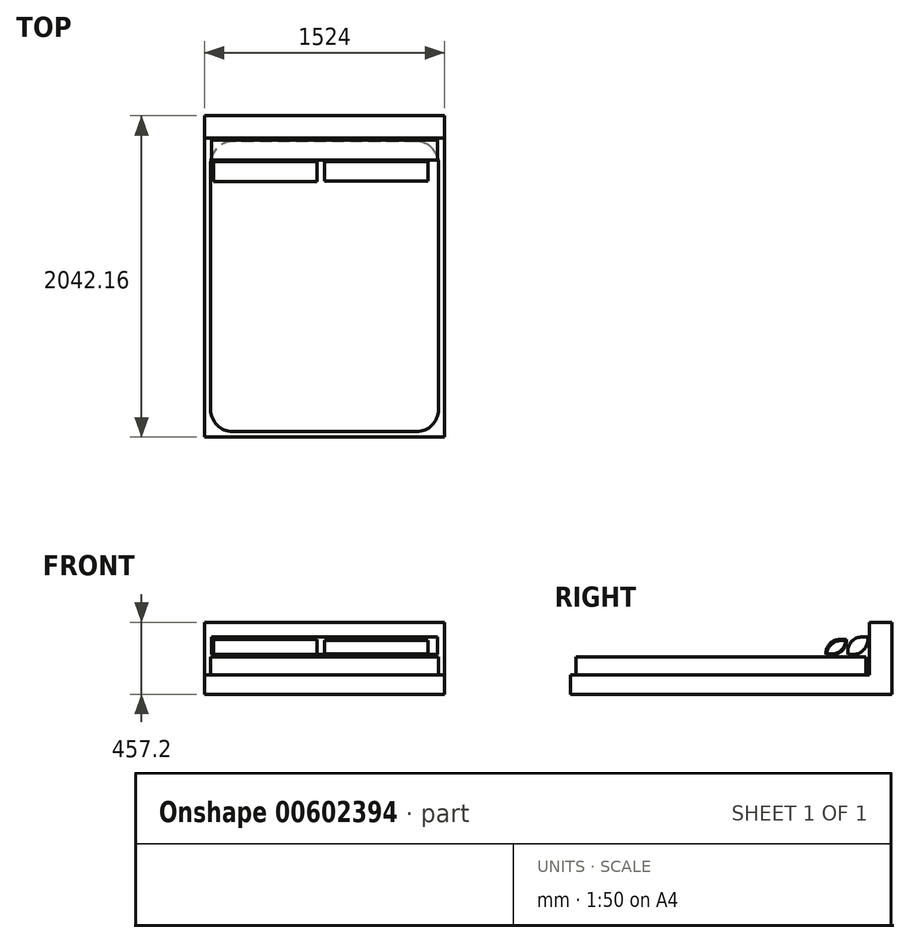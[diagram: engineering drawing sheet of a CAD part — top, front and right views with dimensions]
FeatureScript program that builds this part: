
annotation { "Feature Type Name" : "Feature", "Feature Type Description" : "" }
export const myFeature = defineFeature(function(context is Context, id is Id, definition is map)
    precondition{}
    {
        {
            var Q0;
            Q0=qCreatedBy(makeId("Top.planeOp"),FACE);
            var sketch = newSketch(context, id + "F0", { "sketchPlane" : qUnion([Q0])});
            skLineSegment(sketch, "E0.bottom", {"start": v(-762, 1021.08) * mm, "end": v(762, 1021.08) * mm});
            skLineSegment(sketch, "E0.top", {"start": v(-762, -1021.08) * mm, "end": v(762, -1021.08) * mm});
            skLineSegment(sketch, "E0.left", {"start": v(-762, 1021.08) * mm, "end": v(-762, -1021.08) * mm});
            skLineSegment(sketch, "E0.right", {"start": v(762, 1021.08) * mm, "end": v(762, -1021.08) * mm});
            skPoint(sketch, "E0.middle", {"position": v(0, 0) * mm});
            skSolve(sketch);
        }
        {
            var Q0;
            Q0=makeQuery(id+"F0.imprint","IMPRINT",FACE,{"disambiguationData":[TD([[makeQuery(id+"F0.imprint","IMPRINT",EDGE,{"derivedFrom":sQuery(id+"F0.wireOp",EDGE,"E0.bottom")}),-1.0]])]});
            extrude(context, id + "F1", {"entities" : qUnion([Q0]), "depth" : 121.92 * mm, "offsetDistance" : 30.48 * mm});
        }
        {
            var Q0;
            Q0=makeQuery(id+"F1.opExtrude","CAP_FACE",FACE,{"disambiguationData":[OSD([sQuery(id+"F0.wireOp",EDGE,"E0.bottom"),sQuery(id+"F0.wireOp",EDGE,"E0.top"),sQuery(id+"F0.wireOp",EDGE,"E0.left"),sQuery(id+"F0.wireOp",EDGE,"E0.right")])],"isStart":false});
            var sketch = newSketch(context, id + "F2", { "sketchPlane" : qUnion([Q0])});
            skPoint(sketch, "E1.middle", {"position": v(0, 0) * mm});
            skLineSegment(sketch, "E2.bottom", {"start": v(723.49, -985.48) * mm, "end": v(-723.49, -985.48) * mm});
            skLineSegment(sketch, "E2.top", {"start": v(723.49, 856.5) * mm, "end": v(-723.49, 856.5) * mm});
            skLineSegment(sketch, "E2.left", {"start": v(723.49, -985.48) * mm, "end": v(723.49, 856.5) * mm});
            skLineSegment(sketch, "E2.right", {"start": v(-723.49, -985.48) * mm, "end": v(-723.49, 856.5) * mm});
            skSolve(sketch);
        }
        {
            var Q0;
            Q0=makeQuery(id+"F2.imprint","IMPRINT",FACE,{"disambiguationData":[TD([[makeQuery(id+"F2.imprint","IMPRINT",EDGE,{"derivedFrom":sQuery(id+"F2.wireOp",EDGE,"E2.bottom")}),-1.0]])]});
            extrude(context, id + "F3", {"entities" : qUnion([Q0]), "operationType" : NewBodyOperationType.ADD, "depth" : 114.3 * mm, "offsetDistance" : 30.48 * mm});
        }
        {
            var Q0;
            Q0=makeQuery(id+"F3.opExtrude","SWEPT_EDGE",EDGE,{"disambiguationData":[OSD([sQuery(id+"F2.wireOp",EDGE,"E2.top"),sQuery(id+"F2.wireOp",EDGE,"E2.right")])]});
            var Q1;
            Q1=makeQuery(id+"F3.opExtrude","SWEPT_EDGE",EDGE,{"disambiguationData":[OSD([sQuery(id+"F2.wireOp",EDGE,"E2.top"),sQuery(id+"F2.wireOp",EDGE,"E2.left")])]});
            var Q2;
            Q2=makeQuery(id+"F3.opExtrude","SWEPT_EDGE",EDGE,{"disambiguationData":[OSD([sQuery(id+"F2.wireOp",EDGE,"E2.bottom"),sQuery(id+"F2.wireOp",EDGE,"E2.left")])]});
            var Q3;
            Q3=makeQuery(id+"F3.opExtrude","SWEPT_EDGE",EDGE,{"disambiguationData":[OSD([sQuery(id+"F2.wireOp",EDGE,"E2.bottom"),sQuery(id+"F2.wireOp",EDGE,"E2.right")])]});
            fillet(context, id + "F4", {"entities" : qUnion([Q0, Q1, Q2, Q3]), "radius" : 139.8 * mm, "tangentPropagation" : true, "allowEdgeOverflow" : false});
        }
        {
            var Q0;
            Q0=makeQuery(id+"F1.opExtrude","CAP_FACE",FACE,{"disambiguationData":[OSD([sQuery(id+"F0.wireOp",EDGE,"E0.bottom"),sQuery(id+"F0.wireOp",EDGE,"E0.top"),sQuery(id+"F0.wireOp",EDGE,"E0.left"),sQuery(id+"F0.wireOp",EDGE,"E0.right")])],"isStart":false});
            var sketch = newSketch(context, id + "F5", { "sketchPlane" : qUnion([Q0])});
            skLineSegment(sketch, "E3.bottom", {"start": v(-762, 1021.08) * mm, "end": v(762, 1021.08) * mm});
            skLineSegment(sketch, "E3.top", {"start": v(-762, 877.63) * mm, "end": v(762, 877.63) * mm});
            skLineSegment(sketch, "E3.left", {"start": v(-762, 1021.08) * mm, "end": v(-762, 877.63) * mm});
            skLineSegment(sketch, "E3.right", {"start": v(762, 1021.08) * mm, "end": v(762, 877.63) * mm});
            skSolve(sketch);
        }
        {
            var Q0;
            Q0=makeQuery(id+"F5.imprint","IMPRINT",FACE,{"disambiguationData":[TD([[makeQuery(id+"F5.imprint","IMPRINT",EDGE,{"derivedFrom":sQuery(id+"F5.wireOp",EDGE,"E3.bottom")}),-1.0]])]});
            extrude(context, id + "F6", {"entities" : qUnion([Q0]), "operationType" : NewBodyOperationType.ADD, "depth" : 335.28 * mm, "offsetDistance" : 30.48 * mm});
        }
        {
            var Q0;
            Q0=qCreatedBy(makeId("Right.planeOp"),FACE);
            var sketch = newSketch(context, id + "F7", { "sketchPlane" : qUnion([Q0])});
            skLineSegment(sketch, "E4.bottom", {"start": v(867, 363.9) * mm, "end": v(740.07, 363.9) * mm});
            skLineSegment(sketch, "E4.top", {"start": v(867, 252.83) * mm, "end": v(740.07, 252.83) * mm});
            skLineSegment(sketch, "E4.left", {"start": v(867, 363.9) * mm, "end": v(867, 252.83) * mm});
            skLineSegment(sketch, "E4.right", {"start": v(740.07, 363.9) * mm, "end": v(740.07, 252.83) * mm});
            skSolve(sketch);
        }
        {
            var Q0;
            Q0=makeQuery(id+"F7.imprint","IMPRINT",FACE,{"disambiguationData":[TD([[makeQuery(id+"F7.imprint","IMPRINT",EDGE,{"derivedFrom":sQuery(id+"F7.wireOp",EDGE,"E4.bottom")}),1.0]])]});
            extrude(context, id + "F8", {"entities" : qUnion([Q0]), "endBound" : BoundingType.SYMMETRIC, "depth" : 1432.56 * mm, "offsetDistance" : 30.48 * mm});
        }
        {
            var Q0;
            Q0=makeQuery(id+"F8.opExtrude","SWEPT_EDGE",EDGE,{"disambiguationData":[OSD([sQuery(id+"F7.wireOp",EDGE,"E4.bottom"),sQuery(id+"F7.wireOp",EDGE,"E4.right")])]});
            var Q1;
            Q1=makeQuery(id+"F8.opExtrude","SWEPT_EDGE",EDGE,{"disambiguationData":[OSD([sQuery(id+"F7.wireOp",EDGE,"E4.top"),sQuery(id+"F7.wireOp",EDGE,"E4.left")])]});
            fillet(context, id + "F9", {"entities" : qUnion([Q0, Q1]), "radius" : 91.44 * mm, "tangentPropagation" : true, "allowEdgeOverflow" : false});
        }
        {
            var Q0;
            Q0=qCreatedBy(makeId("Right.planeOp"),FACE);
            var sketch = newSketch(context, id + "F10", { "sketchPlane" : qUnion([Q0])});
            skLineSegment(sketch, "E5.bottom", {"start": v(728.73, 341.23) * mm, "end": v(606.33, 341.23) * mm});
            skLineSegment(sketch, "E5.top", {"start": v(728.73, 255.1) * mm, "end": v(606.33, 255.1) * mm});
            skLineSegment(sketch, "E5.left", {"start": v(728.73, 341.23) * mm, "end": v(728.73, 255.1) * mm});
            skLineSegment(sketch, "E5.right", {"start": v(606.33, 341.23) * mm, "end": v(606.33, 255.1) * mm});
            skSolve(sketch);
        }
        {
            var Q0;
            Q0=makeQuery(id+"F10.imprint","IMPRINT",FACE,{"disambiguationData":[TD([[makeQuery(id+"F10.imprint","IMPRINT",EDGE,{"derivedFrom":sQuery(id+"F10.wireOp",EDGE,"E5.bottom")}),1.0]])]});
            extrude(context, id + "F11", {"entities" : qUnion([Q0]), "depth" : 658.37 * mm, "offsetDistance" : 30.48 * mm});
        }
        {
            var Q0;
            Q0=makeQuery(id+"F11.opExtrude","SWEPT_EDGE",EDGE,{"disambiguationData":[OSD([sQuery(id+"F10.wireOp",EDGE,"E5.bottom"),sQuery(id+"F10.wireOp",EDGE,"E5.right")])]});
            var Q1;
            Q1=makeQuery(id+"F11.opExtrude","SWEPT_EDGE",EDGE,{"disambiguationData":[OSD([sQuery(id+"F10.wireOp",EDGE,"E5.top"),sQuery(id+"F10.wireOp",EDGE,"E5.left")])]});
            fillet(context, id + "F12", {"entities" : qUnion([Q0, Q1]), "radius" : 91.44 * mm, "tangentPropagation" : true, "allowEdgeOverflow" : false});
        }
        {
            var Q0;
            Q0=qCreatedBy(makeId("Right.planeOp"),FACE);
            cPlane(context, id + "F13", {"entities" : qUnion([Q0]), "cplaneType" : CPlaneType.OFFSET, "offset" : 704.1 * mm, "oppositeDirection" : true, "width" : 152.4 * mm, "height" : 152.4 * mm});
        }
        {
            var Q0;
            Q0=qCreatedBy(id+"F13.planeOp",FACE);
            var sketch = newSketch(context, id + "F14", { "sketchPlane" : qUnion([Q0])});
            skLineSegment(sketch, "E6.bottom", {"start": v(731, 347.93) * mm, "end": v(601.8, 347.93) * mm});
            skLineSegment(sketch, "E6.top", {"start": v(731, 252.73) * mm, "end": v(601.8, 252.73) * mm});
            skLineSegment(sketch, "E6.left", {"start": v(731, 347.93) * mm, "end": v(731, 252.73) * mm});
            skLineSegment(sketch, "E6.right", {"start": v(601.8, 347.93) * mm, "end": v(601.8, 252.73) * mm});
            skSolve(sketch);
        }
        {
            var Q0;
            Q0=makeQuery(id+"F14.imprint","IMPRINT",FACE,{"disambiguationData":[TD([[makeQuery(id+"F14.imprint","IMPRINT",EDGE,{"derivedFrom":sQuery(id+"F14.wireOp",EDGE,"E6.bottom")}),1.0]])]});
            extrude(context, id + "F15", {"entities" : qUnion([Q0]), "depth" : 655.32 * mm, "offsetDistance" : 30.48 * mm});
        }
        {
            var Q0;
            Q0=makeQuery(id+"F15.opExtrude","SWEPT_EDGE",EDGE,{"disambiguationData":[OSD([sQuery(id+"F14.wireOp",EDGE,"E6.bottom"),sQuery(id+"F14.wireOp",EDGE,"E6.right")])]});
            var Q1;
            Q1=makeQuery(id+"F15.opExtrude","SWEPT_EDGE",EDGE,{"disambiguationData":[OSD([sQuery(id+"F14.wireOp",EDGE,"E6.top"),sQuery(id+"F14.wireOp",EDGE,"E6.left")])]});
            fillet(context, id + "F16", {"entities" : qUnion([Q0, Q1]), "radius" : 88.4 * mm, "tangentPropagation" : true, "allowEdgeOverflow" : false});
        }
    });
